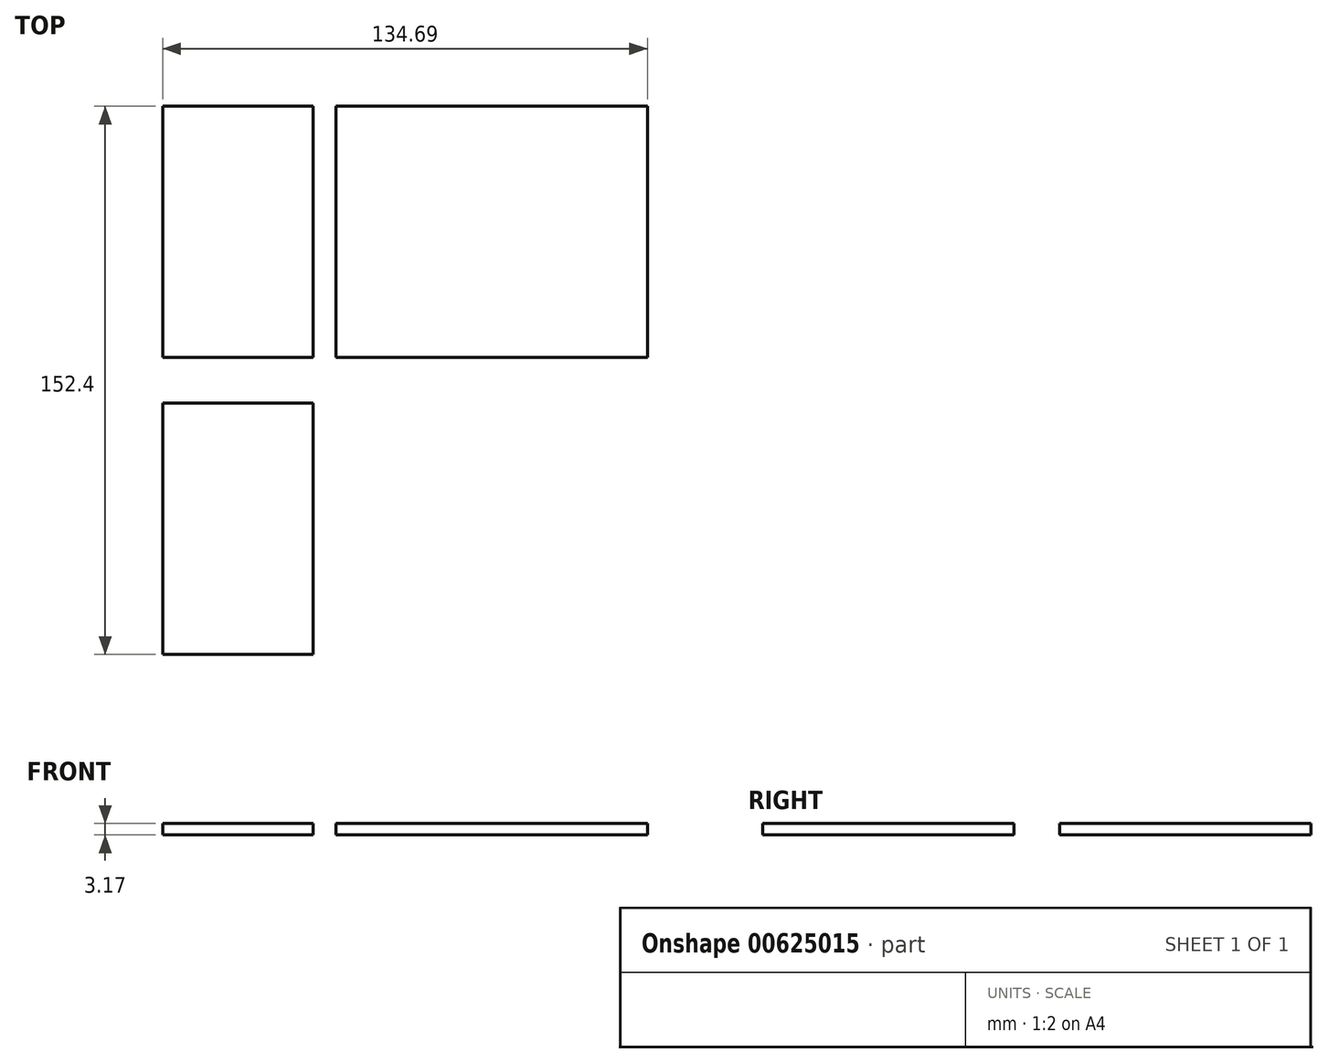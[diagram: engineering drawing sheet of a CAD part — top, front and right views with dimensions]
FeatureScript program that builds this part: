
annotation { "Feature Type Name" : "Feature", "Feature Type Description" : "" }
export const myFeature = defineFeature(function(context is Context, id is Id, definition is map)
    precondition{}
    {
        {
            var Q0;
            Q0=qCreatedBy(makeId("Top.planeOp"),FACE);
            var sketch = newSketch(context, id + "F0", { "sketchPlane" : qUnion([Q0])});
            skLineSegment(sketch, "E0.bottom", {"start": v(0, 0) * mm, "end": v(86.61, 0) * mm});
            skLineSegment(sketch, "E0.top", {"start": v(0, 69.85) * mm, "end": v(86.61, 69.85) * mm});
            skLineSegment(sketch, "E0.left", {"start": v(0, 0) * mm, "end": v(0, 69.85) * mm});
            skLineSegment(sketch, "E0.right", {"start": v(86.61, 0) * mm, "end": v(86.61, 69.85) * mm});
            skLineSegment(sketch, "E1.bottom", {"start": v(0, 69.85) * mm, "end": v(-6.35, 69.85) * mm});
            skLineSegment(sketch, "E1.top", {"start": v(0, -95.25) * mm, "end": v(-6.35, -95.25) * mm});
            skLineSegment(sketch, "E1.left", {"start": v(0, 69.85) * mm, "end": v(0, -95.25) * mm});
            skLineSegment(sketch, "E1.right", {"start": v(-6.35, 69.85) * mm, "end": v(-6.35, -95.25) * mm});
            skLineSegment(sketch, "E2.bottom", {"start": v(-6.35, 69.85) * mm, "end": v(-48.08, 69.85) * mm});
            skLineSegment(sketch, "E2.top", {"start": v(-6.35, 0) * mm, "end": v(-48.08, 0) * mm});
            skLineSegment(sketch, "E2.left", {"start": v(-6.35, 69.85) * mm, "end": v(-6.35, 0) * mm});
            skLineSegment(sketch, "E2.right", {"start": v(-48.08, 69.85) * mm, "end": v(-48.08, 0) * mm});
            skLineSegment(sketch, "E3.bottom", {"start": v(-48.08, 0) * mm, "end": v(-6.35, 0) * mm});
            skLineSegment(sketch, "E3.top", {"start": v(-48.08, -12.7) * mm, "end": v(-6.35, -12.7) * mm});
            skLineSegment(sketch, "E3.left", {"start": v(-48.08, 0) * mm, "end": v(-48.08, -12.7) * mm});
            skLineSegment(sketch, "E3.right", {"start": v(-6.35, 0) * mm, "end": v(-6.35, -12.7) * mm});
            skLineSegment(sketch, "E4.top", {"start": v(-48.08, -82.55) * mm, "end": v(-6.35, -82.55) * mm});
            skLineSegment(sketch, "E4.left", {"start": v(-48.08, -12.7) * mm, "end": v(-48.08, -82.55) * mm});
            skLineSegment(sketch, "E4.right", {"start": v(-6.35, -12.7) * mm, "end": v(-6.35, -82.55) * mm});
            skSolve(sketch);
        }
        {
            var Q0;
            {var subQ0=sQuery(id+"F0.wireOp",EDGE,"E0.bottom");Q0=makeQuery(id+"F0.imprint","IMPRINT",FACE,{"disambiguationData":[TD([[makeQuery(id+"F0.imprint","IMPRINT",EDGE,{"derivedFrom":subQ0}),1.0]])]});}
            var Q1;
            Q1=makeQuery(id+"F0.imprint","IMPRINT",FACE,{"disambiguationData":[TD([[makeQuery(id+"F0.imprint","IMPRINT",EDGE,{"derivedFrom":sQuery(id+"F0.wireOp",EDGE,"E2.bottom")}),1.0]])]});
            var Q2;
            Q2=makeQuery(id+"F0.imprint","IMPRINT",FACE,{"disambiguationData":[TD([[makeQuery(id+"F0.imprint","IMPRINT",EDGE,{"derivedFrom":sQuery(id+"F0.wireOp",EDGE,"E3.top")}),-1.0]])]});
            extrude(context, id + "F1", {"entities" : qUnion([Q0, Q1, Q2]), "depth" : 3.17 * mm, "offsetDistance" : 25.4 * mm});
        }
    });
